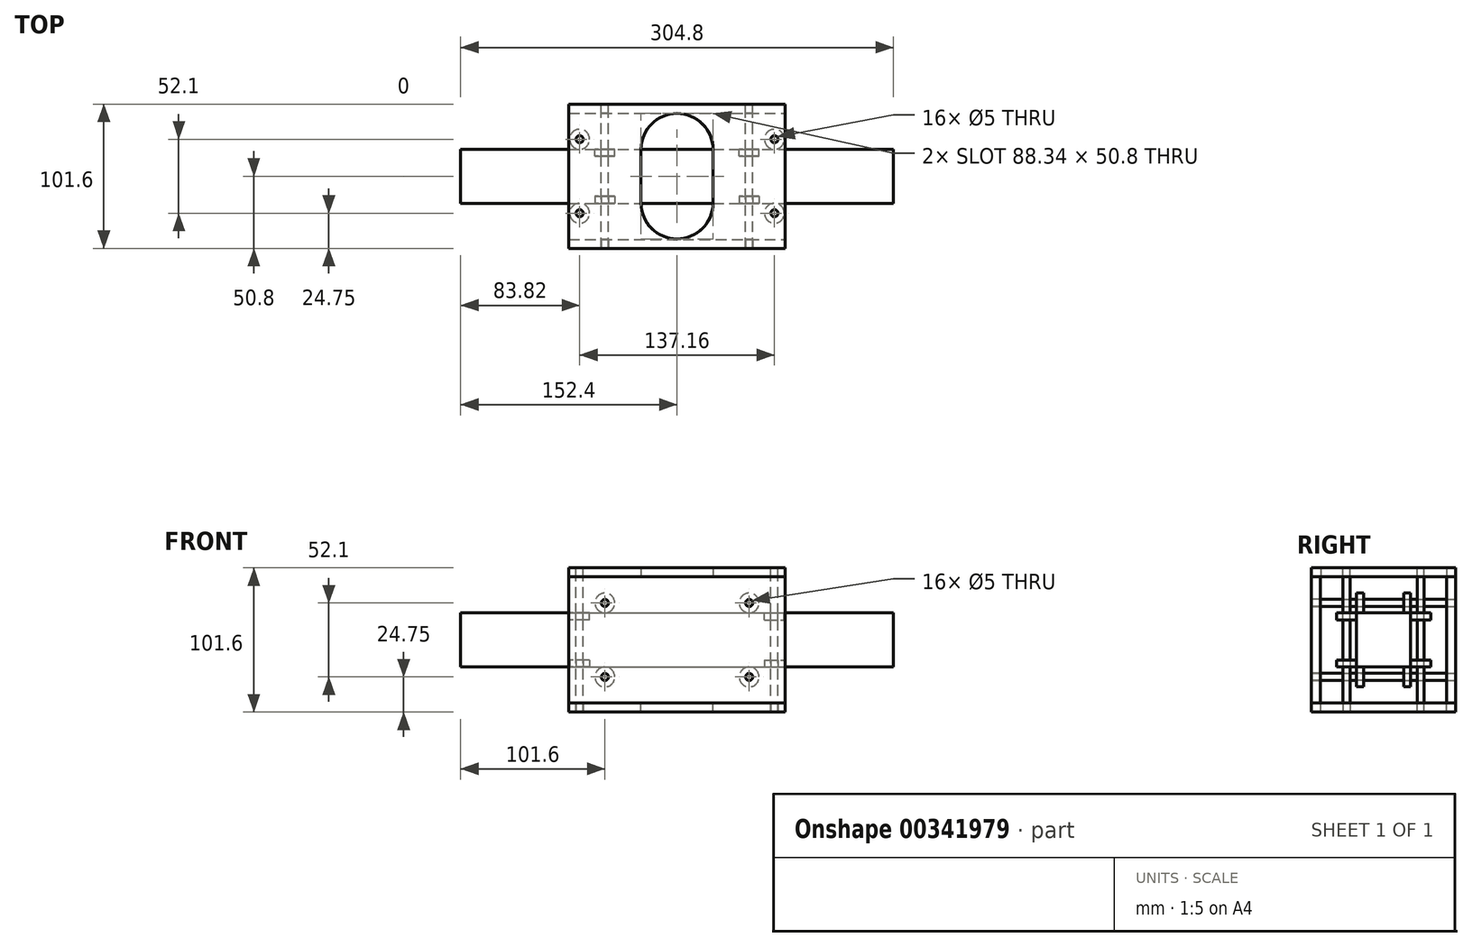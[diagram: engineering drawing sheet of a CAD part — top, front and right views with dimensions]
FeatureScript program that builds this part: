
annotation { "Feature Type Name" : "Feature", "Feature Type Description" : "" }
export const myFeature = defineFeature(function(context is Context, id is Id, definition is map)
    precondition{}
    {
        {
            var Q0;
            Q0=qCreatedBy(makeId("Front.planeOp"),FACE);
            var sketch = newSketch(context, id + "F0", { "sketchPlane" : qUnion([Q0])});
            skLineSegment(sketch, "E0.bottom", {"start": v(-152.4, 19.05) * mm, "end": v(152.4, 19.05) * mm});
            skLineSegment(sketch, "E0.top", {"start": v(-152.4, -19.05) * mm, "end": v(152.4, -19.05) * mm});
            skLineSegment(sketch, "E0.left", {"start": v(-152.4, 19.05) * mm, "end": v(-152.4, -19.05) * mm});
            skLineSegment(sketch, "E0.right", {"start": v(152.4, 19.05) * mm, "end": v(152.4, -19.05) * mm});
            skPoint(sketch, "E0.middle", {"position": v(0, 0) * mm});
            skSolve(sketch);
        }
        {
            var Q0;
            Q0=makeQuery(id+"F0.imprint","IMPRINT",FACE,{"disambiguationData":[TD([[makeQuery(id+"F0.imprint","IMPRINT",EDGE,{"derivedFrom":sQuery(id+"F0.wireOp",EDGE,"E0.bottom")}),-1.0]])]});
            extrude(context, id + "F1", {"entities" : qUnion([Q0]), "endBound" : BoundingType.SYMMETRIC, "depth" : 38.1 * mm});
        }
        {
            var Q0;
            Q0=makeQuery(id+"F1.opExtrude","CAP_FACE",FACE,{"disambiguationData":[OSD([sQuery(id+"F0.wireOp",EDGE,"E0.bottom"),sQuery(id+"F0.wireOp",EDGE,"E0.top"),sQuery(id+"F0.wireOp",EDGE,"E0.left"),sQuery(id+"F0.wireOp",EDGE,"E0.right")])],"isStart":false});
            var sketch = newSketch(context, id + "F2", { "sketchPlane" : qUnion([Q0])});
            skCircle(sketch, "E1", {"center": v(-50.8, 26.05) * mm, "radius": 7 * mm});
            skCircle(sketch, "E2", {"center": v(-50.8, 26.05) * mm, "radius": 2.5 * mm});
            skCircle(sketch, "E3", {"center": v(50.8, 26.05) * mm, "radius": 7 * mm});
            skCircle(sketch, "E4", {"center": v(50.8, 26.05) * mm, "radius": 2.5 * mm});
            skSolve(sketch);
        }
        {
            var Q0;
            Q0=makeQuery(id+"F2.imprint","IMPRINT",FACE,{"disambiguationData":[TD([[makeQuery(id+"F2.imprint","IMPRINT",EDGE,{"derivedFrom":sQuery(id+"F2.wireOp",EDGE,"E1")}),1.0]])]});
            var Q1;
            Q1=makeQuery(id+"F2.imprint","IMPRINT",FACE,{"disambiguationData":[TD([[makeQuery(id+"F2.imprint","IMPRINT",EDGE,{"derivedFrom":sQuery(id+"F2.wireOp",EDGE,"E3")}),1.0]])]});
            extrude(context, id + "F3", {"entities" : qUnion([Q0, Q1]), "oppositeDirection" : true, "depth" : 5 * mm});
        }
        {
            var Q0;
            Q0=makeQuery(id+"F3.opExtrude","SWEPT_BODY",BODY,{"disambiguationData":[OSD([sQuery(id+"F2.wireOp",EDGE,"E1"),sQuery(id+"F2.wireOp",EDGE,"E2")])]});
            var Q1;
            Q1=makeQuery(id+"F3.opExtrude","SWEPT_BODY",BODY,{"disambiguationData":[OSD([sQuery(id+"F2.wireOp",EDGE,"E3"),sQuery(id+"F2.wireOp",EDGE,"E4")])]});
            var Q2;
            Q2=qCreatedBy(makeId("Front.planeOp"),FACE);
            mirror(context, id + "F4", {"operationType" : NewBodyOperationType.ADD, "entities" : qUnion([Q0, Q1]), "mirrorPlane" : qUnion([Q2])});
        }
        {
            var Q0;
            Q0=makeQuery(id+"F3.opExtrude","SWEPT_BODY",BODY,{"disambiguationData":[OSD([sQuery(id+"F2.wireOp",EDGE,"E3"),sQuery(id+"F2.wireOp",EDGE,"E4")])]});
            var Q1;
            Q1=makeQuery(id+"F4.opPattern","COPY",BODY,{"derivedFrom":makeQuery(id+"F3.opExtrude","SWEPT_BODY",BODY,{"disambiguationData":[OSD([sQuery(id+"F2.wireOp",EDGE,"E3"),sQuery(id+"F2.wireOp",EDGE,"E4")])]}),"instanceName":"1"});
            var Q2;
            Q2=makeQuery(id+"F3.opExtrude","SWEPT_BODY",BODY,{"disambiguationData":[OSD([sQuery(id+"F2.wireOp",EDGE,"E1"),sQuery(id+"F2.wireOp",EDGE,"E2")])]});
            var Q3;
            Q3=makeQuery(id+"F4.opPattern","COPY",BODY,{"derivedFrom":makeQuery(id+"F3.opExtrude","SWEPT_BODY",BODY,{"disambiguationData":[OSD([sQuery(id+"F2.wireOp",EDGE,"E1"),sQuery(id+"F2.wireOp",EDGE,"E2")])]}),"instanceName":"1"});
            var Q4;
            Q4=qCreatedBy(makeId("Top.planeOp"),FACE);
            mirror(context, id + "F5", {"operationType" : NewBodyOperationType.ADD, "entities" : qUnion([Q0, Q1, Q2, Q3]), "mirrorPlane" : qUnion([Q4])});
        }
        {
            var Q0;
            Q0=qCreatedBy(makeId("Front.planeOp"),FACE);
            var sketch = newSketch(context, id + "F6", { "sketchPlane" : qUnion([Q0])});
            skCircle(sketch, "E5.0", {"center": v(-50.8, 26.05) * mm, "radius": 2.5 * mm});
            skSolve(sketch);
        }
        {
            var Q0;
            Q0=makeQuery(id+"F6.imprint","IMPRINT",FACE,{"disambiguationData":[TD([[makeQuery(id+"F6.imprint","IMPRINT",EDGE,{"derivedFrom":sQuery(id+"F6.wireOp",EDGE,"E5.0")}),1.0]])]});
            extrude(context, id + "F7", {"entities" : qUnion([Q0]), "endBound" : BoundingType.SYMMETRIC, "depth" : 101.6 * mm});
        }
        {
            var Q0;
            Q0=makeQuery(id+"F7.opExtrude","SWEPT_BODY",BODY,{"disambiguationData":[OSD([sQuery(id+"F6.wireOp",EDGE,"E5.0")])]});
            var Q1;
            Q1=qCreatedBy(makeId("Right.planeOp"),FACE);
            mirror(context, id + "F8", {"entities" : qUnion([Q0]), "mirrorPlane" : qUnion([Q1])});
        }
        {
            var Q0;
            Q0=makeQuery(id+"F8.opPattern","COPY",BODY,{"derivedFrom":makeQuery(id+"F7.opExtrude","SWEPT_BODY",BODY,{"disambiguationData":[OSD([sQuery(id+"F6.wireOp",EDGE,"E5.0")])]}),"instanceName":"1"});
            var Q1;
            Q1=makeQuery(id+"F7.opExtrude","SWEPT_BODY",BODY,{"disambiguationData":[OSD([sQuery(id+"F6.wireOp",EDGE,"E5.0")])]});
            var Q2;
            Q2=qCreatedBy(makeId("Top.planeOp"),FACE);
            mirror(context, id + "F9", {"entities" : qUnion([Q0, Q1]), "mirrorPlane" : qUnion([Q2])});
        }
        {
            var Q0;
            Q0=makeQuery(id+"F7.opExtrude","CAP_FACE",FACE,{"disambiguationData":[OSD([sQuery(id+"F6.wireOp",EDGE,"E5.0")])],"isStart":false});
            var sketch = newSketch(context, id + "F10", { "sketchPlane" : qUnion([Q0])});
            skCircle(sketch, "E6.0", {"center": v(-50.8, 26.05) * mm, "radius": 2.5 * mm});
            skCircle(sketch, "E7.0", {"center": v(-50.8, -26.05) * mm, "radius": 2.5 * mm});
            skCircle(sketch, "E8.0", {"center": v(50.8, 26.05) * mm, "radius": 2.5 * mm});
            skCircle(sketch, "E9.0", {"center": v(50.8, -26.05) * mm, "radius": 2.5 * mm});
            skLineSegment(sketch, "E10.bottom", {"start": v(-76.2, 44.45) * mm, "end": v(76.2, 44.45) * mm});
            skLineSegment(sketch, "E10.top", {"start": v(-76.2, -44.45) * mm, "end": v(76.2, -44.45) * mm});
            skLineSegment(sketch, "E10.left", {"start": v(-76.2, 44.45) * mm, "end": v(-76.2, -44.45) * mm});
            skLineSegment(sketch, "E10.right", {"start": v(76.2, 44.45) * mm, "end": v(76.2, -44.45) * mm});
            skPoint(sketch, "E10.middle", {"position": v(0, 0) * mm});
            skSolve(sketch);
        }
        {
            var Q0;
            Q0=makeQuery(id+"F10.imprint","IMPRINT",FACE,{"disambiguationData":[TD([[makeQuery(id+"F10.imprint","IMPRINT",EDGE,{"derivedFrom":sQuery(id+"F10.wireOp",EDGE,"E6.0")}),-1.0]])]});
            extrude(context, id + "F11", {"entities" : qUnion([Q0]), "oppositeDirection" : true, "depth" : 6.35 * mm});
        }
        {
            var Q0;
            Q0=makeQuery(id+"F11.opExtrude","SWEPT_BODY",BODY,{"disambiguationData":[OSD([sQuery(id+"F10.wireOp",EDGE,"E6.0"),sQuery(id+"F10.wireOp",EDGE,"E7.0"),sQuery(id+"F10.wireOp",EDGE,"E8.0"),sQuery(id+"F10.wireOp",EDGE,"E9.0"),sQuery(id+"F10.wireOp",EDGE,"E10.bottom"),sQuery(id+"F10.wireOp",EDGE,"E10.top"),sQuery(id+"F10.wireOp",EDGE,"E10.left"),sQuery(id+"F10.wireOp",EDGE,"E10.right")])]});
            var Q1;
            Q1=qCreatedBy(makeId("Front.planeOp"),FACE);
            mirror(context, id + "F12", {"entities" : qUnion([Q0]), "mirrorPlane" : qUnion([Q1])});
        }
        {
            var Q0;
            Q0=makeQuery(id+"F12.opPattern","COPY",FACE,{"derivedFrom":makeQuery(id+"F11.opExtrude","SWEPT_FACE",FACE,{"disambiguationData":[OSD([sQuery(id+"F10.wireOp",EDGE,"E10.bottom")])]}),"instanceName":"1"});
            var sketch = newSketch(context, id + "F13", { "sketchPlane" : qUnion([Q0])});
            skPoint(sketch, "E11.0", {"position": v(76.2, -50.8) * mm});
            skLineSegment(sketch, "E12.bottom", {"start": v(-76.2, 50.8) * mm, "end": v(76.2, 50.8) * mm});
            skLineSegment(sketch, "E12.top", {"start": v(-76.2, -50.8) * mm, "end": v(76.2, -50.8) * mm});
            skLineSegment(sketch, "E12.left", {"start": v(-76.2, 50.8) * mm, "end": v(-76.2, -50.8) * mm});
            skLineSegment(sketch, "E12.right", {"start": v(76.2, 50.8) * mm, "end": v(76.2, -50.8) * mm});
            skLineSegment(sketch, "E13.left", {"start": v(-25.4, 18.77) * mm, "end": v(-25.4, -18.77) * mm});
            skLineSegment(sketch, "E13.right", {"start": v(25.4, 18.77) * mm, "end": v(25.4, -18.77) * mm});
            skPoint(sketch, "E13.middle", {"position": v(0, 0) * mm});
            skArc(sketch, "E14", {"start": v(25.4, 18.77) * mm, "mid": v(0, 44.17) * mm, "end": v(-25.4, 18.77) * mm});
            skArc(sketch, "E15.MirrorCS", {"start": v(25.4, -18.77) * mm, "mid": v(0, -44.17) * mm, "end": v(-25.4, -18.77) * mm});
            skSolve(sketch);
        }
        {
            var Q0;
            {var subQ0=sQuery(id+"F13.wireOp",EDGE,"E12.top");Q0=makeQuery(id+"F13.imprint","IMPRINT",FACE,{"disambiguationData":[TD([[makeQuery(id+"F13.imprint","IMPRINT",EDGE,{"derivedFrom":subQ0}),1.0]])]});}
            var Q1;
            {var subQ0=sQuery(id+"F13.wireOp",EDGE,"E12.bottom");Q1=makeQuery(id+"F13.imprint","IMPRINT",FACE,{"disambiguationData":[TD([[makeQuery(id+"F13.imprint","IMPRINT",EDGE,{"derivedFrom":subQ0}),-1.0]])]});}
            extrude(context, id + "F14", {"entities" : qUnion([Q0, Q1]), "depth" : 6.35 * mm});
        }
        {
            var Q0;
            Q0=makeQuery(id+"F1.opExtrude","SWEPT_FACE",FACE,{"disambiguationData":[OSD([sQuery(id+"F0.wireOp",EDGE,"E0.bottom")])]});
            var sketch = newSketch(context, id + "F15", { "sketchPlane" : qUnion([Q0])});
            skCircle(sketch, "E16", {"center": v(-68.58, 26.05) * mm, "radius": 7 * mm});
            skCircle(sketch, "E17", {"center": v(-68.58, 26.05) * mm, "radius": 2.5 * mm});
            skSolve(sketch);
        }
        {
            var Q0;
            Q0=makeQuery(id+"F15.imprint","IMPRINT",FACE,{"disambiguationData":[TD([[makeQuery(id+"F15.imprint","IMPRINT",EDGE,{"derivedFrom":sQuery(id+"F15.wireOp",EDGE,"E16")}),1.0]])]});
            extrude(context, id + "F16", {"entities" : qUnion([Q0]), "oppositeDirection" : true, "depth" : 5 * mm});
        }
        {
            var Q0;
            Q0=makeQuery(id+"F16.opExtrude","SWEPT_BODY",BODY,{"disambiguationData":[OSD([sQuery(id+"F15.wireOp",EDGE,"E16"),sQuery(id+"F15.wireOp",EDGE,"E17")])]});
            var Q1;
            Q1=qCreatedBy(makeId("Top.planeOp"),FACE);
            mirror(context, id + "F17", {"operationType" : NewBodyOperationType.ADD, "entities" : qUnion([Q0]), "mirrorPlane" : qUnion([Q1])});
        }
        {
            var Q0;
            Q0=makeQuery(id+"F17.opPattern","COPY",BODY,{"derivedFrom":makeQuery(id+"F16.opExtrude","SWEPT_BODY",BODY,{"disambiguationData":[OSD([sQuery(id+"F15.wireOp",EDGE,"E16"),sQuery(id+"F15.wireOp",EDGE,"E17")])]}),"instanceName":"1"});
            var Q1;
            Q1=makeQuery(id+"F16.opExtrude","SWEPT_BODY",BODY,{"disambiguationData":[OSD([sQuery(id+"F15.wireOp",EDGE,"E16"),sQuery(id+"F15.wireOp",EDGE,"E17")])]});
            var Q2;
            Q2=qCreatedBy(makeId("Right.planeOp"),FACE);
            mirror(context, id + "F18", {"operationType" : NewBodyOperationType.ADD, "entities" : qUnion([Q0, Q1]), "mirrorPlane" : qUnion([Q2])});
        }
        {
            var Q0;
            Q0=makeQuery(id+"F17.opPattern","COPY",BODY,{"derivedFrom":makeQuery(id+"F16.opExtrude","SWEPT_BODY",BODY,{"disambiguationData":[OSD([sQuery(id+"F15.wireOp",EDGE,"E16"),sQuery(id+"F15.wireOp",EDGE,"E17")])]}),"instanceName":"1"});
            var Q1;
            Q1=makeQuery(id+"F16.opExtrude","SWEPT_BODY",BODY,{"disambiguationData":[OSD([sQuery(id+"F15.wireOp",EDGE,"E16"),sQuery(id+"F15.wireOp",EDGE,"E17")])]});
            var Q2;
            Q2=makeQuery(id+"F18.opPattern","COPY",BODY,{"derivedFrom":makeQuery(id+"F17.opPattern","COPY",BODY,{"derivedFrom":makeQuery(id+"F16.opExtrude","SWEPT_BODY",BODY,{"disambiguationData":[OSD([sQuery(id+"F15.wireOp",EDGE,"E16"),sQuery(id+"F15.wireOp",EDGE,"E17")])]}),"instanceName":"1"}),"instanceName":"1"});
            var Q3;
            Q3=makeQuery(id+"F18.opPattern","COPY",BODY,{"derivedFrom":makeQuery(id+"F16.opExtrude","SWEPT_BODY",BODY,{"disambiguationData":[OSD([sQuery(id+"F15.wireOp",EDGE,"E16"),sQuery(id+"F15.wireOp",EDGE,"E17")])]}),"instanceName":"1"});
            var Q4;
            Q4=qCreatedBy(makeId("Front.planeOp"),FACE);
            mirror(context, id + "F19", {"operationType" : NewBodyOperationType.ADD, "entities" : qUnion([Q0, Q1, Q2, Q3]), "mirrorPlane" : qUnion([Q4])});
        }
        {
            var Q0;
            Q0=makeQuery(id+"F14.opExtrude","CAP_FACE",FACE,{"disambiguationData":[OSD([sQuery(id+"F13.wireOp",EDGE,"E12.bottom"),sQuery(id+"F13.wireOp",EDGE,"E12.top"),sQuery(id+"F13.wireOp",EDGE,"E12.left"),sQuery(id+"F13.wireOp",EDGE,"E12.right")])],"isStart":false});
            var sketch = newSketch(context, id + "F20", { "sketchPlane" : qUnion([Q0])});
            skCircle(sketch, "E18.0", {"center": v(-68.58, 26.05) * mm, "radius": 2.5 * mm});
            skCircle(sketch, "E19.0", {"center": v(-68.58, -26.05) * mm, "radius": 2.5 * mm});
            skCircle(sketch, "E20.0", {"center": v(68.58, 26.05) * mm, "radius": 2.5 * mm});
            skCircle(sketch, "E21.0", {"center": v(68.58, -26.05) * mm, "radius": 2.5 * mm});
            skSolve(sketch);
        }
        {
            var Q0;
            Q0=makeQuery(id+"F20.imprint","IMPRINT",FACE,{"disambiguationData":[TD([[makeQuery(id+"F20.imprint","IMPRINT",EDGE,{"derivedFrom":sQuery(id+"F20.wireOp",EDGE,"E18.0")}),1.0]])]});
            var Q1;
            Q1=makeQuery(id+"F20.imprint","IMPRINT",FACE,{"disambiguationData":[TD([[makeQuery(id+"F20.imprint","IMPRINT",EDGE,{"derivedFrom":sQuery(id+"F20.wireOp",EDGE,"E19.0")}),1.0]])]});
            var Q2;
            Q2=makeQuery(id+"F20.imprint","IMPRINT",FACE,{"disambiguationData":[TD([[makeQuery(id+"F20.imprint","IMPRINT",EDGE,{"derivedFrom":sQuery(id+"F20.wireOp",EDGE,"E20.0")}),1.0]])]});
            var Q3;
            Q3=makeQuery(id+"F20.imprint","IMPRINT",FACE,{"disambiguationData":[TD([[makeQuery(id+"F20.imprint","IMPRINT",EDGE,{"derivedFrom":sQuery(id+"F20.wireOp",EDGE,"E21.0")}),1.0]])]});
            var Q4;
            Q4=makeQuery(id+"F22.opPattern","COPY",FACE,{"derivedFrom":makeQuery(id+"F14.opExtrude","CAP_FACE",FACE,{"disambiguationData":[OSD([sQuery(id+"F13.wireOp",EDGE,"E12.bottom"),sQuery(id+"F13.wireOp",EDGE,"E12.top"),sQuery(id+"F13.wireOp",EDGE,"E12.left"),sQuery(id+"F13.wireOp",EDGE,"E12.right")])],"isStart":false}),"instanceName":"1"});
            extrude(context, id + "F21", {"entities" : qUnion([Q0, Q1, Q2, Q3]), "operationType" : NewBodyOperationType.REMOVE, "endBound" : BoundingType.UP_TO_NEXT, "oppositeDirection" : true, "endBoundEntityFace" : qUnion([Q4]), "depth" : 231.65 * mm});
        }
        {
            var Q0;
            Q0=makeQuery(id+"F14.opExtrude","SWEPT_BODY",BODY,{"disambiguationData":[OSD([sQuery(id+"F13.wireOp",EDGE,"E12.bottom"),sQuery(id+"F13.wireOp",EDGE,"E12.top"),sQuery(id+"F13.wireOp",EDGE,"E12.left"),sQuery(id+"F13.wireOp",EDGE,"E12.right")])]});
            var Q1;
            Q1=qCreatedBy(makeId("Top.planeOp"),FACE);
            mirror(context, id + "F22", {"entities" : qUnion([Q0]), "mirrorPlane" : qUnion([Q1])});
        }
        {
            var Q0;
            Q0=makeQuery(id+"F14.opExtrude","CAP_FACE",FACE,{"disambiguationData":[OSD([sQuery(id+"F13.wireOp",EDGE,"E12.bottom"),sQuery(id+"F13.wireOp",EDGE,"E12.top"),sQuery(id+"F13.wireOp",EDGE,"E12.left"),sQuery(id+"F13.wireOp",EDGE,"E12.right")])],"isStart":false});
            var sketch = newSketch(context, id + "F23", { "sketchPlane" : qUnion([Q0])});
            skCircle(sketch, "E22.0", {"center": v(-68.58, 26.05) * mm, "radius": 2.5 * mm});
            skCircle(sketch, "E23.0", {"center": v(-68.58, -26.05) * mm, "radius": 2.5 * mm});
            skCircle(sketch, "E24.0", {"center": v(68.58, -26.05) * mm, "radius": 2.5 * mm});
            skCircle(sketch, "E25.0", {"center": v(68.58, 26.05) * mm, "radius": 2.5 * mm});
            skSolve(sketch);
        }
        {
            var Q0;
            Q0=makeQuery(id+"F23.imprint","IMPRINT",FACE,{"disambiguationData":[TD([[makeQuery(id+"F23.imprint","IMPRINT",EDGE,{"derivedFrom":sQuery(id+"F23.wireOp",EDGE,"E22.0")}),1.0]])]});
            var Q1;
            Q1=makeQuery(id+"F23.imprint","IMPRINT",FACE,{"disambiguationData":[TD([[makeQuery(id+"F23.imprint","IMPRINT",EDGE,{"derivedFrom":sQuery(id+"F23.wireOp",EDGE,"E23.0")}),1.0]])]});
            var Q2;
            Q2=makeQuery(id+"F23.imprint","IMPRINT",FACE,{"disambiguationData":[TD([[makeQuery(id+"F23.imprint","IMPRINT",EDGE,{"derivedFrom":sQuery(id+"F23.wireOp",EDGE,"E24.0")}),1.0]])]});
            var Q3;
            Q3=makeQuery(id+"F23.imprint","IMPRINT",FACE,{"disambiguationData":[TD([[makeQuery(id+"F23.imprint","IMPRINT",EDGE,{"derivedFrom":sQuery(id+"F23.wireOp",EDGE,"E25.0")}),1.0]])]});
            var Q4;
            Q4=makeQuery(id+"F22.opPattern","COPY",FACE,{"derivedFrom":makeQuery(id+"F14.opExtrude","CAP_FACE",FACE,{"disambiguationData":[OSD([sQuery(id+"F13.wireOp",EDGE,"E12.bottom"),sQuery(id+"F13.wireOp",EDGE,"E12.top"),sQuery(id+"F13.wireOp",EDGE,"E12.left"),sQuery(id+"F13.wireOp",EDGE,"E12.right")])],"isStart":false}),"instanceName":"1"});
            extrude(context, id + "F24", {"entities" : qUnion([Q0, Q1, Q2, Q3]), "endBound" : BoundingType.UP_TO_SURFACE, "oppositeDirection" : true, "endBoundEntityFace" : qUnion([Q4]), "depth" : 25.4 * mm});
        }
    });
